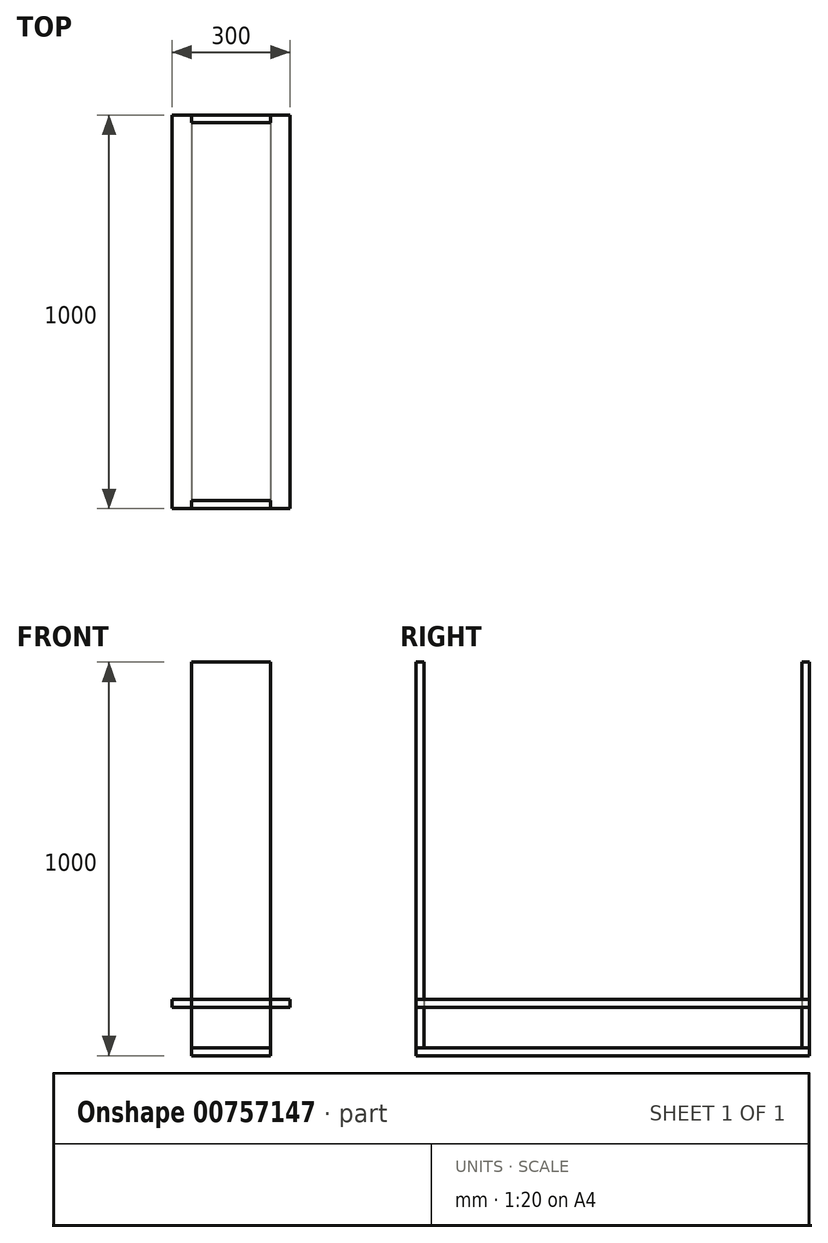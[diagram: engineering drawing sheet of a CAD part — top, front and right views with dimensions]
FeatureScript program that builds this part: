
annotation { "Feature Type Name" : "Feature", "Feature Type Description" : "" }
export const myFeature = defineFeature(function(context is Context, id is Id, definition is map)
    precondition{}
    {
        {
            var Q0;
            Q0=qCreatedBy(makeId("Top.planeOp"),FACE);
            var sketch = newSketch(context, id + "F0", { "sketchPlane" : qUnion([Q0])});
            skLineSegment(sketch, "E0.bottom", {"start": v(0, 0) * mm, "end": v(200, 0) * mm});
            skLineSegment(sketch, "E0.top", {"start": v(0, 1000) * mm, "end": v(200, 1000) * mm});
            skLineSegment(sketch, "E0.left", {"start": v(0, 0) * mm, "end": v(0, 1000) * mm});
            skLineSegment(sketch, "E0.right", {"start": v(200, 0) * mm, "end": v(200, 1000) * mm});
            skLineSegment(sketch, "E1.top", {"start": v(0, 20) * mm, "end": v(200, 20) * mm});
            skLineSegment(sketch, "E1.left", {"start": v(0, 0) * mm, "end": v(0, 20) * mm});
            skLineSegment(sketch, "E1.right", {"start": v(200, 0) * mm, "end": v(200, 20) * mm});
            skLineSegment(sketch, "E2.top", {"start": v(0, 980) * mm, "end": v(200, 980) * mm});
            skLineSegment(sketch, "E2.left", {"start": v(0, 1000) * mm, "end": v(0, 980) * mm});
            skLineSegment(sketch, "E2.right", {"start": v(200, 1000) * mm, "end": v(200, 980) * mm});
            skSolve(sketch);
        }
        {
            var Q0;
            {var subQ0=sQuery(id+"F0.wireOp",EDGE,"E0.bottom");Q0=makeQuery(id+"F0.imprint","IMPRINT",FACE,{"disambiguationData":[TD([[makeQuery(id+"F0.imprint","IMPRINT",EDGE,{"derivedFrom":subQ0}),1.0]])]});}
            var Q1;
            {var subQ0=sQuery(id+"F0.wireOp",EDGE,"E0.top");Q1=makeQuery(id+"F0.imprint","IMPRINT",FACE,{"disambiguationData":[TD([[makeQuery(id+"F0.imprint","IMPRINT",EDGE,{"derivedFrom":subQ0}),-1.0]])]});}
            extrude(context, id + "F1", {"entities" : qUnion([Q0, Q1]), "depth" : 1000 * mm, "offsetDistance" : 25 * mm});
        }
        {
            var Q0;
            Q0=makeQuery(id+"F1.opExtrude","SWEPT_FACE",FACE,{"disambiguationData":[OSD([sQuery(id+"F0.wireOp",EDGE,"E0.bottom")])]});
            var sketch = newSketch(context, id + "F2", { "sketchPlane" : qUnion([Q0])});
            skLineSegment(sketch, "E3.bottom", {"start": v(0, 0) * mm, "end": v(200, 0) * mm});
            skLineSegment(sketch, "E3.top", {"start": v(0, 20.36) * mm, "end": v(200, 20.36) * mm});
            skLineSegment(sketch, "E3.left", {"start": v(0, 0) * mm, "end": v(0, 20.36) * mm});
            skLineSegment(sketch, "E3.right", {"start": v(200, 0) * mm, "end": v(200, 20.36) * mm});
            skLineSegment(sketch, "E4", {"start": v(0, 122.86) * mm, "end": v(-50, 122.86) * mm});
            skLineSegment(sketch, "E5.bottom", {"start": v(-50, 122.86) * mm, "end": v(250, 122.86) * mm});
            skLineSegment(sketch, "E5.top", {"start": v(-50, 142.86) * mm, "end": v(250, 142.86) * mm});
            skLineSegment(sketch, "E5.left", {"start": v(-50, 122.86) * mm, "end": v(-50, 142.86) * mm});
            skLineSegment(sketch, "E5.right", {"start": v(250, 122.86) * mm, "end": v(250, 142.86) * mm});
            skSolve(sketch);
        }
        {
            var Q0;
            Q0=makeQuery(id+"F2.imprint","IMPRINT",FACE,{"disambiguationData":[TD([[makeQuery(id+"F2.imprint","IMPRINT",EDGE,{"derivedFrom":sQuery(id+"F2.wireOp",EDGE,"E3.bottom")}),1.0]])]});
            extrude(context, id + "F3", {"entities" : qUnion([Q0]), "operationType" : NewBodyOperationType.ADD, "depth" : -1000 * mm, "offsetDistance" : 25 * mm});
        }
        {
            var Q0;
            Q0 = qSketchRegion(id + "F2", true);
            extrude(context, id + "F4", {"entities" : qUnion([Q0]), "depth" : -1000 * mm, "offsetDistance" : 25 * mm});
        }
    });
